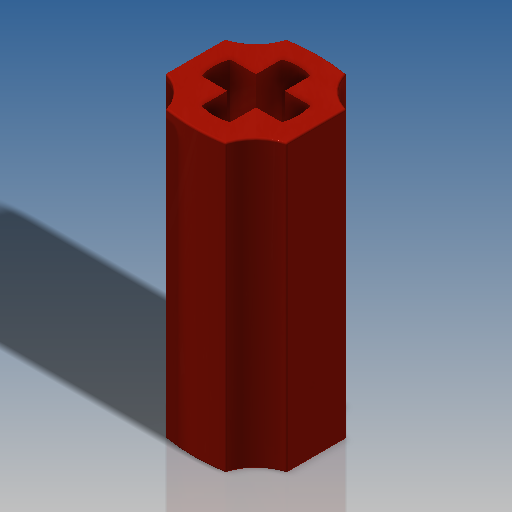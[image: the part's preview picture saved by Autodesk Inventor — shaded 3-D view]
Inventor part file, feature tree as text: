
AUTODESK INVENTOR PART (.ipt)
format: ipt  version: 2018.3 (Build 223284000, 284)  size: 253,440 bytes
history: native  units: in
note: dims shown in document units (in); Inventor stores cm internally (conversion verified against a paired STEP export)
features: extrude x2, sketch x1, fillet x1
ambient origin geometry x8: Origin, YZ Plane, XZ Plane, XY Plane, X Axis, Y Axis, Z Axis, Center Point
bodies: Solid1 (feature_tree)
feature tree (4):
  sketch  "Sketch2"  dims[d0=0.1873in d1=0.2772in d2=0.315in d4=0.063in d5=0.6299in d6=0.0in d19=0.0039in d20=0.189in d21=0.7441in d22=0.2677in d23=0.0079in d24=0.0in d25=0.0in]
  extrude  "Extrusion1"  Depth=0.0079in
  extrude  "Extrusion3"  Depth=0.315in
  fillet  "Fillet1"  Radius=0.063in
